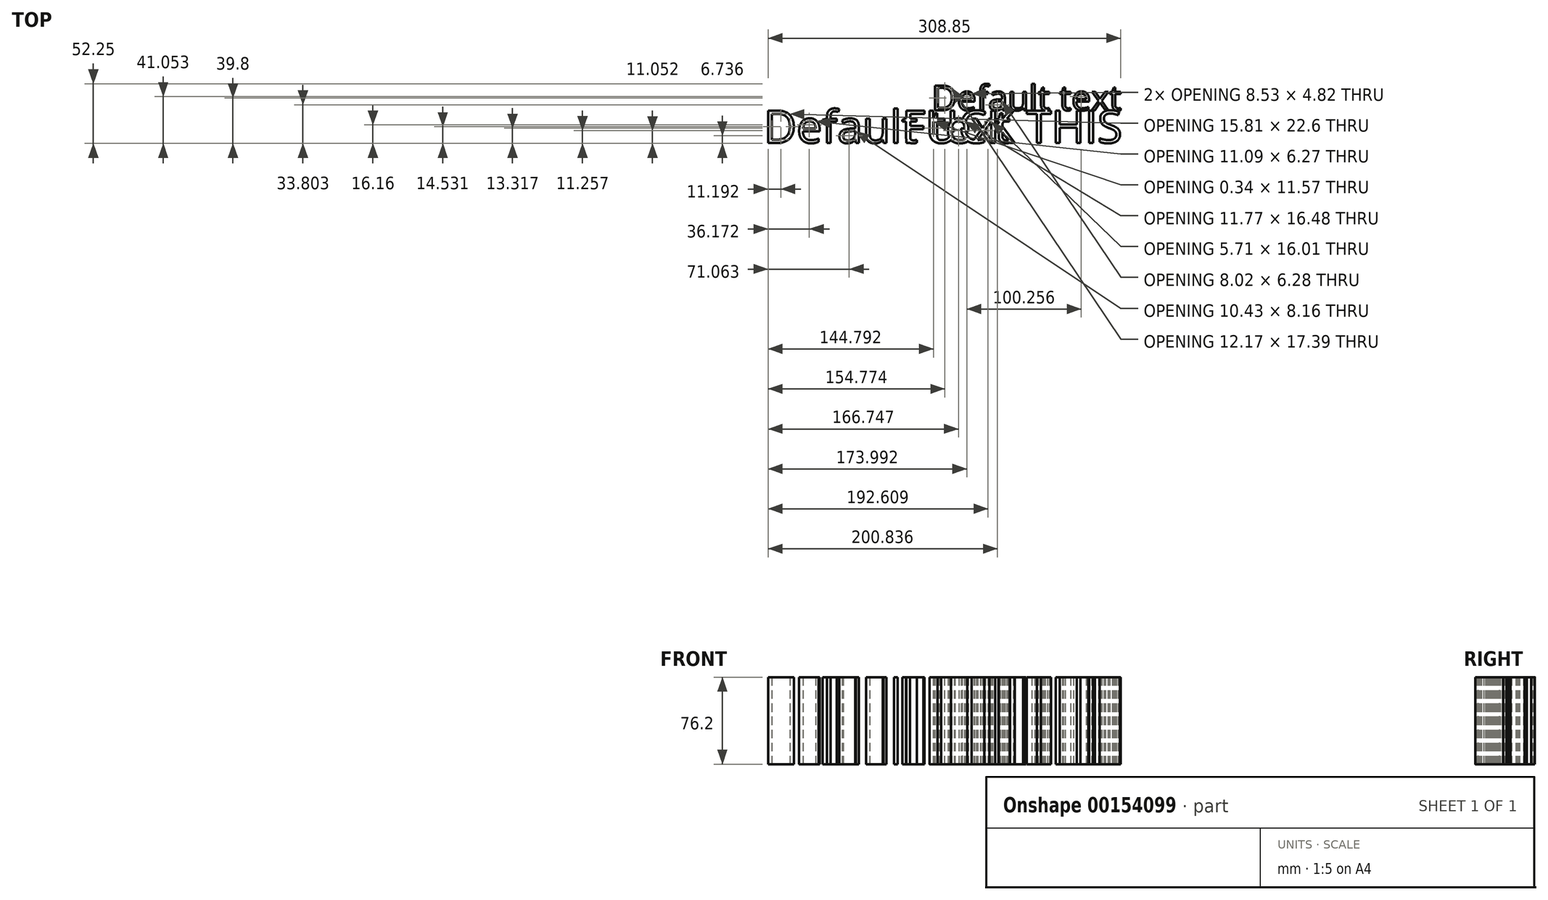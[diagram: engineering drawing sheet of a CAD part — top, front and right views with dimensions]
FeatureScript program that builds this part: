
annotation { "Feature Type Name" : "Feature", "Feature Type Description" : "" }
export const myFeature = defineFeature(function(context is Context, id is Id, definition is map)
    precondition{}
    {
        {
            var Q0;
            Q0=qCreatedBy(makeId("Top.planeOp"),FACE);
            var sketch = newSketch(context, id + "F0", { "sketchPlane" : qUnion([Q0])});
            skText(sketch, "E0", { "text": "FUCK THIS", "fontName": "OpenSans-Regular.ttf"});
            skText(sketch, "E1", { "text": "Default text", "fontName": "OpenSans-Regular.ttf"});
            skText(sketch, "E2", { "text": "Default text", "fontName": "OpenSans-Regular.ttf"});
            const initialGuessF0  = {"E0": [-0.02203, 0, 1, 0, 0.02853], "E1": [-0.1432, 0, 1, 0, 0.02853], "E2": [0.00386, 0.02853, 1, 0, 0.02195]};
            skSetInitialGuess(sketch, initialGuessF0);
            skSolve(sketch);
        }
        {
            var Q0;
            Q0 = qSketchRegion(id + "F0", true);
            extrude(context, id + "F1", {"entities" : qUnion([Q0]), "depth" : 76.2 * mm});
        }
    });
